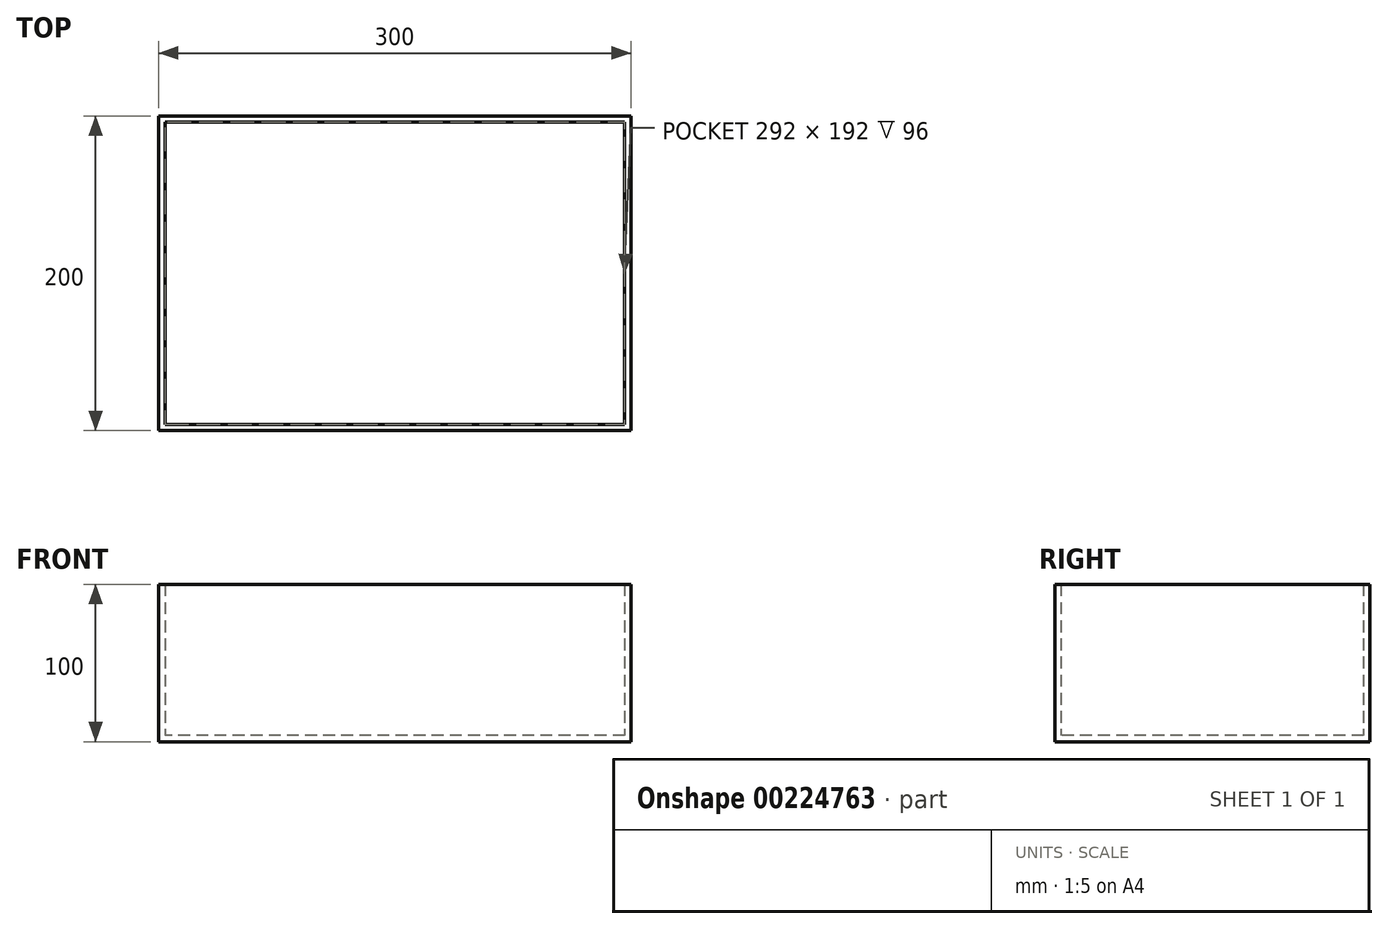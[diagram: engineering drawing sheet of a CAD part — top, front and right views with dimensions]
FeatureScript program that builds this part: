
annotation { "Feature Type Name" : "Feature", "Feature Type Description" : "" }
export const myFeature = defineFeature(function(context is Context, id is Id, definition is map)
    precondition{}
    {
        {
            var Q0;
            Q0=qCreatedBy(makeId("Top.planeOp"),FACE);
            var sketch = newSketch(context, id + "F0", { "sketchPlane" : qUnion([Q0])});
            skLineSegment(sketch, "E0.bottom", {"start": v(150, 100) * mm, "end": v(-150, 100) * mm});
            skLineSegment(sketch, "E0.top", {"start": v(150, -100) * mm, "end": v(-150, -100) * mm});
            skLineSegment(sketch, "E0.left", {"start": v(150, 100) * mm, "end": v(150, -100) * mm});
            skLineSegment(sketch, "E0.right", {"start": v(-150, 100) * mm, "end": v(-150, -100) * mm});
            skPoint(sketch, "E0.middle", {"position": v(0, 0) * mm});
            skSolve(sketch);
        }
        {
            var Q0;
            Q0=makeQuery(id+"F0.imprint","IMPRINT",FACE,{"disambiguationData":[TD([[makeQuery(id+"F0.imprint","IMPRINT",EDGE,{"derivedFrom":sQuery(id+"F0.wireOp",EDGE,"E0.bottom")}),1.0]])]});
            extrude(context, id + "F1", {"entities" : qUnion([Q0]), "depth" : 100 * mm, "symmetric" : true});
        }
        {
            var Q0;
            Q0=makeQuery(id+"F1.opExtrude","CAP_FACE",FACE,{"disambiguationData":[OSD([sQuery(id+"F0.wireOp",EDGE,"E0.bottom"),sQuery(id+"F0.wireOp",EDGE,"E0.top"),sQuery(id+"F0.wireOp",EDGE,"E0.left"),sQuery(id+"F0.wireOp",EDGE,"E0.right")])],"isStart":false});
            shell(context, id + "F2", {"entities" : qUnion([Q0]), "thickness" : 4 * mm});
        }
    });
